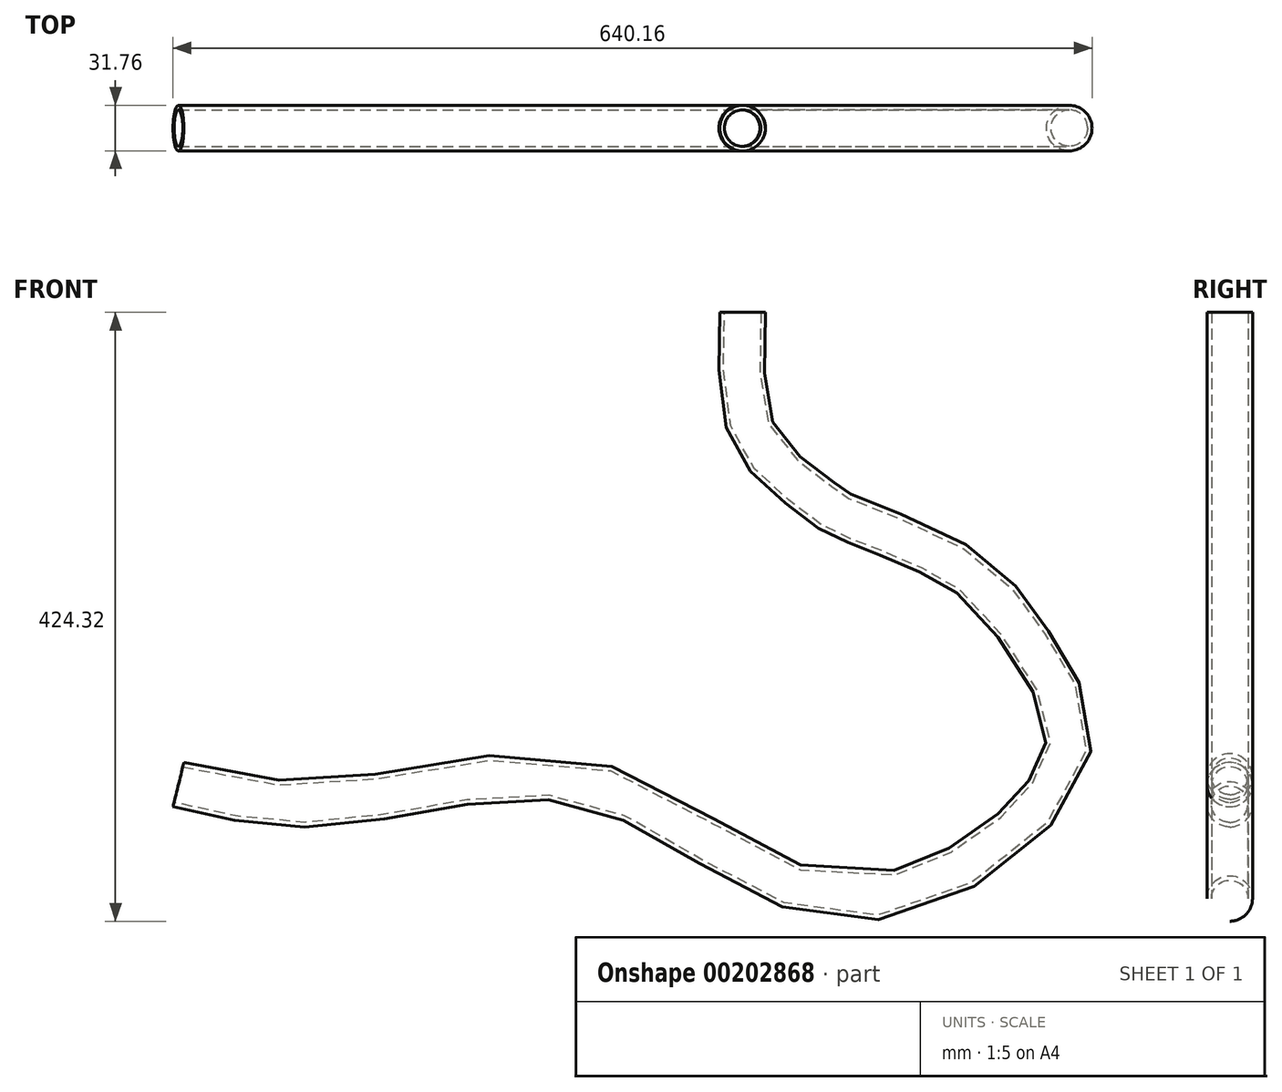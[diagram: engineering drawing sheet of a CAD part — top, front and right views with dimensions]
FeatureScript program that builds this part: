
annotation { "Feature Type Name" : "Feature", "Feature Type Description" : "" }
export const myFeature = defineFeature(function(context is Context, id is Id, definition is map)
    precondition{}
    {
        {
            var Q0;
            Q0=qCreatedBy(makeId("Top.planeOp"),FACE);
            var sketch = newSketch(context, id + "F0", { "sketchPlane" : qUnion([Q0])});
            skCircle(sketch, "E0", {"center": v(0, 0) * mm, "radius": 12.7 * mm});
            skCircle(sketch, "E1", {"center": v(0, 0) * mm, "radius": 15.88 * mm});
            skSolve(sketch);
        }
        {
            var Q0;
            Q0=qCreatedBy(makeId("Front.planeOp"),FACE);
            var sketch = newSketch(context, id + "F1", { "sketchPlane" : qUnion([Q0])});
            skFitSpline(sketch, "E2", {"points": [v(0, 0) * mm, v(9.26, -88.55) * mm, v(53.57, -130.73) * mm, v(66.19, -140) * mm, v(152.46, -178.66) * mm, v(202.62, -235.23) * mm, v(225.02, -311) * mm, v(77.36, -408.44) * mm, v(-104.15, -328.94) * mm, v(-284.38, -341.85) * mm, v(-392.94, -329.14) * mm], "startDerivative": vector(0, -968.87) * mm, "endDerivative": vector(-938.86, 229.57) * mm});
            skSolve(sketch);
        }
        {
            var Q0;
            Q0=makeQuery(id+"F0.imprint","IMPRINT",FACE,{"disambiguationData":[TD([[makeQuery(id+"F0.imprint","IMPRINT",EDGE,{"derivedFrom":sQuery(id+"F0.wireOp",EDGE,"E0")}),-1.0]])]});
            var Q1;
            Q1=sQuery(id+"F1.wireOp",EDGE,"E2");
            sweep(context, id + "F2", {"profiles" : qUnion([Q0]), "path" : qUnion([Q1])});
        }
    });
